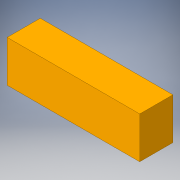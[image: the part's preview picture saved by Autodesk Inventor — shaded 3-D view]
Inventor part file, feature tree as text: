
AUTODESK INVENTOR PART (.ipt)
format: ipt  version: 2016 (Build 200138000, 138)  size: 92,160 bytes
history: native  units: in
note: dims shown in document units (in); Inventor stores cm internally (conversion verified against a paired STEP export)
features: extrude x1, sketch x1
ambient origin geometry x8: Origin, YZ Plane, XZ Plane, XY Plane, X Axis, Y Axis, Z Axis, Center Point
bodies: Solid1 (feature_tree)
feature tree (2):
  extrude  "Extrusion1"  Depth=1.25in
  sketch  "Sketch1"  dims[d0=4.0in d1=1.25in d2=1.0in d3=0.0in]
